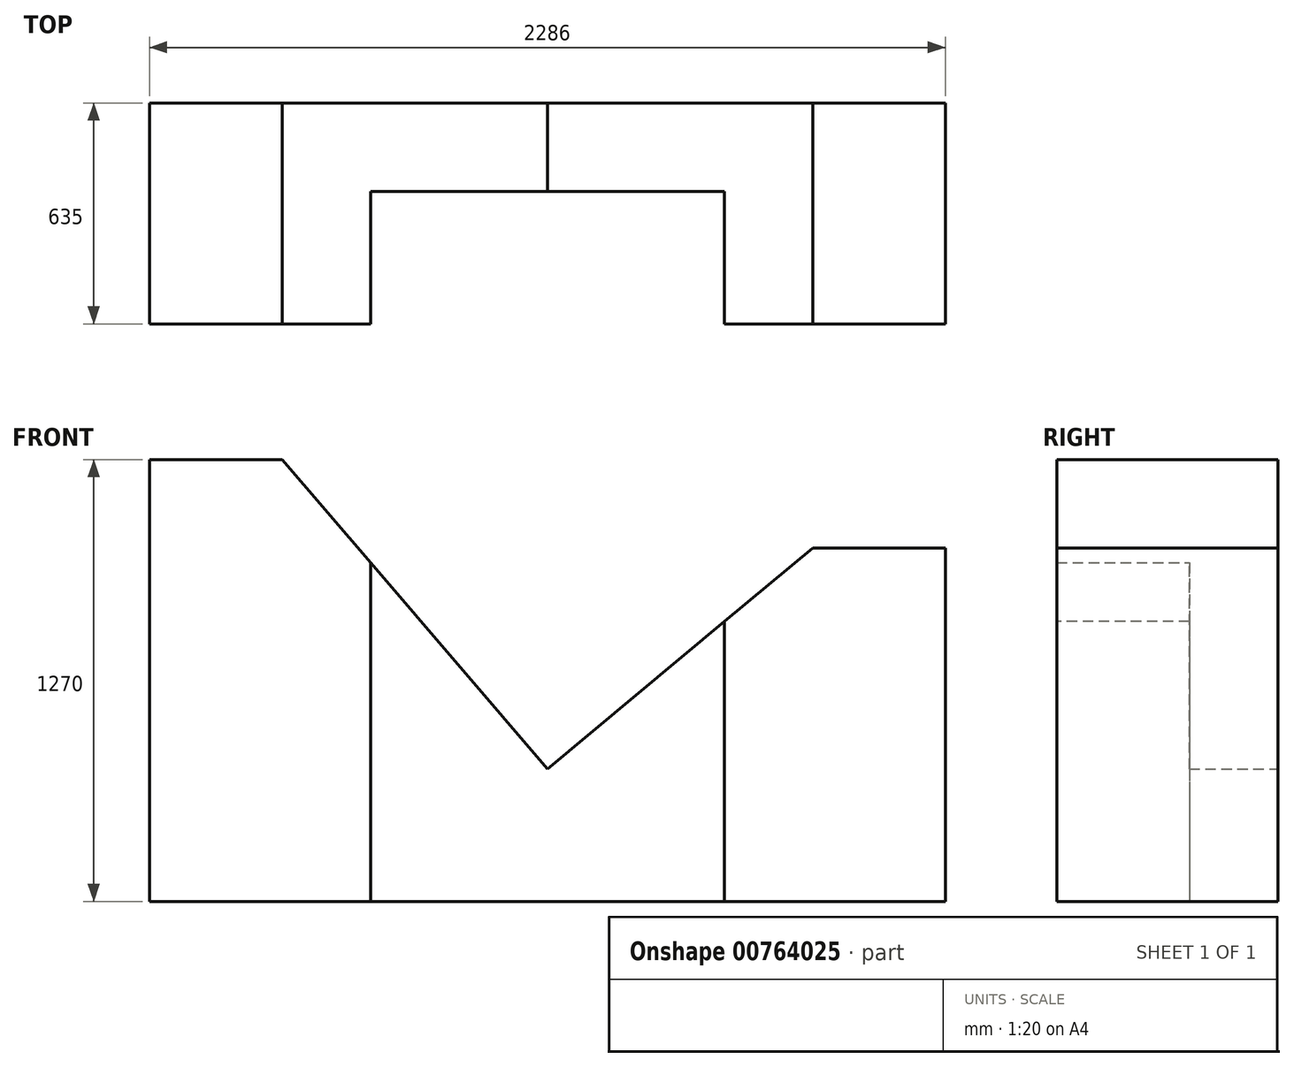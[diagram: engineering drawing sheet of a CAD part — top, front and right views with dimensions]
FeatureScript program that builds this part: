
annotation { "Feature Type Name" : "Feature", "Feature Type Description" : "" }
export const myFeature = defineFeature(function(context is Context, id is Id, definition is map)
    precondition{}
    {
        {
            var Q0;
            Q0=qCreatedBy(makeId("Front.planeOp"),FACE);
            var sketch = newSketch(context, id + "F0", { "sketchPlane" : qUnion([Q0])});
            skLineSegment(sketch, "E0.bottom", {"start": v(0, 0) * mm, "end": v(2286, 0) * mm});
            skLineSegment(sketch, "E0.top", {"start": v(0, 1270) * mm, "end": v(2286, 1270) * mm});
            skLineSegment(sketch, "E0.left", {"start": v(0, 0) * mm, "end": v(0, 1270) * mm});
            skLineSegment(sketch, "E0.right", {"start": v(2286, 0) * mm, "end": v(2286, 1270) * mm});
            skSolve(sketch);
        }
        {
            var Q0;
            Q0=makeQuery(id+"F0.imprint","IMPRINT",FACE,{"disambiguationData":[TD([[makeQuery(id+"F0.imprint","IMPRINT",EDGE,{"derivedFrom":sQuery(id+"F0.wireOp",EDGE,"E0.bottom")}),1.0]])]});
            extrude(context, id + "F1", {"entities" : qUnion([Q0]), "depth" : 635 * mm, "offsetDistance" : 25.4 * mm});
        }
        {
            var Q0;
            Q0=makeQuery(id+"F1.opExtrude","CAP_FACE",FACE,{"disambiguationData":[OSD([sQuery(id+"F0.wireOp",EDGE,"E0.bottom"),sQuery(id+"F0.wireOp",EDGE,"E0.top"),sQuery(id+"F0.wireOp",EDGE,"E0.left"),sQuery(id+"F0.wireOp",EDGE,"E0.right")])],"isStart":false});
            var sketch = newSketch(context, id + "F2", { "sketchPlane" : qUnion([Q0])});
            skLineSegment(sketch, "E1", {"start": v(0, 1270) * mm, "end": v(635, 1270) * mm});
            skLineSegment(sketch, "E2", {"start": v(635, 1270) * mm, "end": v(635, 0) * mm});
            skLineSegment(sketch, "E3", {"start": v(2286, 1270) * mm, "end": v(1651, 1270) * mm});
            skLineSegment(sketch, "E4", {"start": v(1651, 1270) * mm, "end": v(1651, 0) * mm});
            skLineSegment(sketch, "E5", {"start": v(1651, 0) * mm, "end": v(2286, 0) * mm});
            skSolve(sketch);
        }
        {
            var Q0;
            {var subQ0=sQuery(id+"F2.wireOp",EDGE,"E2");Q0=makeQuery(id+"F2.imprint","IMPRINT",FACE,{"disambiguationData":[TD([[makeQuery(id+"F2.imprint","IMPRINT",EDGE,{"derivedFrom":subQ0}),1.0]])]});}
            extrude(context, id + "F3", {"entities" : qUnion([Q0]), "operationType" : NewBodyOperationType.REMOVE, "oppositeDirection" : true, "depth" : 381 * mm, "offsetDistance" : 25.4 * mm});
        }
        {
            var Q0;
            Q0=makeQuery(id+"F1.opExtrude","CAP_FACE",FACE,{"disambiguationData":[OSD([sQuery(id+"F0.wireOp",EDGE,"E0.bottom"),sQuery(id+"F0.wireOp",EDGE,"E0.top"),sQuery(id+"F0.wireOp",EDGE,"E0.left"),sQuery(id+"F0.wireOp",EDGE,"E0.right")])],"isStart":true});
            var sketch = newSketch(context, id + "F4", { "sketchPlane" : qUnion([Q0])});
            skLineSegment(sketch, "E6", {"start": v(0, 1270) * mm, "end": v(-381, 1270) * mm});
            skLineSegment(sketch, "E7", {"start": v(-381, 1270) * mm, "end": v(-1143, 381) * mm});
            skLineSegment(sketch, "E8", {"start": v(-1143, 381) * mm, "end": v(-1143, 0) * mm});
            skLineSegment(sketch, "E9", {"start": v(-2286, 1016) * mm, "end": v(-1905, 1016) * mm});
            skLineSegment(sketch, "E10", {"start": v(-1905, 1016) * mm, "end": v(-1905, 0) * mm});
            skLineSegment(sketch, "E11", {"start": v(-1905, 1016) * mm, "end": v(-1143, 381) * mm});
            skLineSegment(sketch, "E12", {"start": v(-1143, 0) * mm, "end": v(0, 0) * mm});
            skSolve(sketch);
        }
        {
            var Q0;
            {var subQ3=sQuery(id+"F4.wireOp",EDGE,"E7");Q0=makeQuery(id+"F4.imprint","IMPRINT",FACE,{"disambiguationData":[TD([[makeQuery(id+"F4.imprint","IMPRINT",EDGE,{"derivedFrom":subQ3}),-1.0]])]});}
            extrude(context, id + "F5", {"entities" : qUnion([Q0]), "operationType" : NewBodyOperationType.REMOVE, "oppositeDirection" : true, "depth" : 635 * mm, "offsetDistance" : 25.4 * mm});
        }
    });
